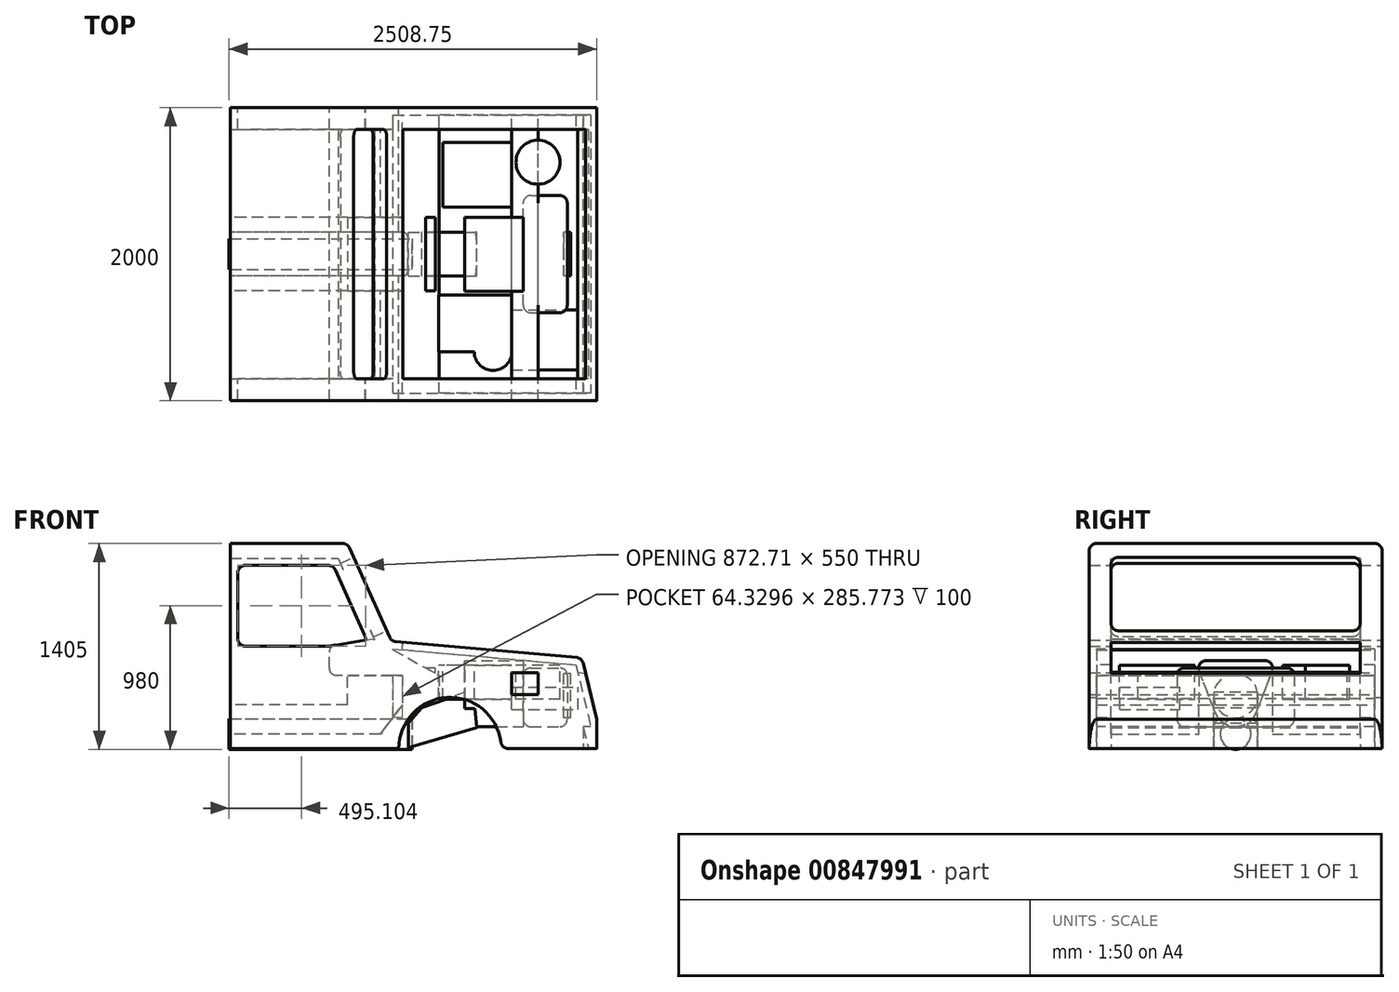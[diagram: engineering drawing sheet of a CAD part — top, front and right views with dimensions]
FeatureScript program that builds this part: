
annotation { "Feature Type Name" : "Feature", "Feature Type Description" : "" }
export const myFeature = defineFeature(function(context is Context, id is Id, definition is map)
    precondition{}
    {
        {
            var Q0;
            Q0=qCreatedBy(makeId("Front.planeOp"),FACE);
            var sketch = newSketch(context, id + "F0", { "sketchPlane" : qUnion([Q0])});
            skLineSegment(sketch, "E0", {"start": v(0, 1700) * mm, "end": v(767.65, 1700) * mm});
            skLineSegment(sketch, "E1", {"start": v(813.26, 1670.49) * mm, "end": v(1087.98, 1058.9) * mm});
            skLineSegment(sketch, "E2", {"start": v(1129.23, 1029.59) * mm, "end": v(2364.1, 921.55) * mm});
            skLineSegment(sketch, "E3", {"start": v(2408.38, 883.36) * mm, "end": v(2500, 500) * mm});
            skLineSegment(sketch, "E4", {"start": v(2500, 300) * mm, "end": v(1896.86, 300) * mm});
            skArc(sketch, "E5", {"start": v(1847.25, 343.75) * mm, "mid": v(1500, 650) * mm, "end": v(1152.75, 343.75) * mm});
            skLineSegment(sketch, "E6", {"start": v(1103.14, 300) * mm, "end": v(0, 300) * mm});
            skLineSegment(sketch, "E7", {"start": v(0, 1700) * mm, "end": v(0, 300) * mm});
            skLineSegment(sketch, "E8", {"start": v(100, 1550) * mm, "end": v(670.59, 1550) * mm});
            skLineSegment(sketch, "E9", {"start": v(716.2, 1520.49) * mm, "end": v(918.34, 1070.49) * mm});
            skLineSegment(sketch, "E10", {"start": v(872.73, 1000) * mm, "end": v(100, 1000) * mm});
            skLineSegment(sketch, "E11", {"start": v(50, 1500) * mm, "end": v(50, 1050) * mm});
            skPoint(sketch, "E12.orphan", {"position": v(0, 1000) * mm});
            skLineSegment(sketch, "E13", {"start": v(2500, 500) * mm, "end": v(2500, 300) * mm});
            skLineSegment(sketch, "E14", {"start": v(1100, 1032.14) * mm, "end": v(2504.74, 1032.14) * mm, "construction": true});
            skPoint(sketch, "E15.visualSharp", {"position": v(2400, 918.4) * mm});
            skArc(sketch, "E15.filletArc", {"start": v(2408.38, 883.36) * mm, "mid": v(2392.4, 909.6) * mm, "end": v(2364.1, 921.55) * mm});
            skPoint(sketch, "E16.visualSharp", {"position": v(1100, 1032.14) * mm});
            skArc(sketch, "E16.filletArc", {"start": v(1087.98, 1058.9) * mm, "mid": v(1104.62, 1038.64) * mm, "end": v(1129.23, 1029.59) * mm});
            skPoint(sketch, "E17.visualSharp", {"position": v(800, 1700) * mm});
            skArc(sketch, "E17.filletArc", {"start": v(813.26, 1670.49) * mm, "mid": v(794.8, 1691.98) * mm, "end": v(767.65, 1700) * mm});
            skPoint(sketch, "E18.visualSharp", {"position": v(702.94, 1550) * mm});
            skArc(sketch, "E18.filletArc", {"start": v(716.2, 1520.49) * mm, "mid": v(697.75, 1541.98) * mm, "end": v(670.59, 1550) * mm});
            skPoint(sketch, "E19.visualSharp", {"position": v(950, 1000) * mm});
            skArc(sketch, "E19.filletArc", {"start": v(872.73, 1000) * mm, "mid": v(914.7, 1022.84) * mm, "end": v(918.34, 1070.49) * mm});
            skPoint(sketch, "E20.visualSharp", {"position": v(50, 1000) * mm});
            skArc(sketch, "E20.filletArc", {"start": v(50, 1050) * mm, "mid": v(64.64, 1014.64) * mm, "end": v(100, 1000) * mm});
            skPoint(sketch, "E21.visualSharp", {"position": v(50, 1550) * mm});
            skArc(sketch, "E21.filletArc", {"start": v(100, 1550) * mm, "mid": v(64.64, 1535.36) * mm, "end": v(50, 1500) * mm});
            skPoint(sketch, "E22.visualSharp", {"position": v(1850, 300) * mm});
            skArc(sketch, "E22.filletArc", {"start": v(1847.25, 343.75) * mm, "mid": v(1863.8, 312.5) * mm, "end": v(1896.86, 300) * mm});
            skPoint(sketch, "E23.visualSharp", {"position": v(1150, 300) * mm});
            skArc(sketch, "E23.filletArc", {"start": v(1103.14, 300) * mm, "mid": v(1136.2, 312.5) * mm, "end": v(1152.75, 343.75) * mm});
            skSolve(sketch);
        }
        {
            var Q0;
            Q0=makeQuery(id+"F0.imprint","IMPRINT",FACE,{"disambiguationData":[TD([[makeQuery(id+"F0.imprint","IMPRINT",EDGE,{"derivedFrom":sQuery(id+"F0.wireOp",EDGE,"E0")}),-1.0]])]});
            extrude(context, id + "F1", {"entities" : qUnion([Q0]), "endBound" : BoundingType.SYMMETRIC, "depth" : 2000 * mm, "offsetDistance" : 25 * mm});
        }
        {
            var Q0;
            Q0=qCreatedBy(makeId("Front.planeOp"),FACE);
            var sketch = newSketch(context, id + "F2", { "sketchPlane" : qUnion([Q0])});
            skLineSegment(sketch, "E24", {"start": v(0, 1600) * mm, "end": v(735.3, 1600) * mm});
            skLineSegment(sketch, "E25", {"start": v(735.3, 1600) * mm, "end": v(1032.83, 937.64) * mm});
            skLineSegment(sketch, "E26", {"start": v(1032.83, 937.64) * mm, "end": v(2319.5, 825.07) * mm});
            skLineSegment(sketch, "E27", {"start": v(2319.5, 825.07) * mm, "end": v(2444.98, 300) * mm});
            skLineSegment(sketch, "E28", {"start": v(2444.98, 300) * mm, "end": v(0, 300) * mm});
            skLineSegment(sketch, "E29", {"start": v(0, 300) * mm, "end": v(0, 1600) * mm});
            skSolve(sketch);
        }
        {
            var Q0;
            Q0 = qSketchRegion(id + "F2", true);
            extrude(context, id + "F3", {"entities" : qUnion([Q0]), "operationType" : NewBodyOperationType.REMOVE, "endBound" : BoundingType.SYMMETRIC, "oppositeDirection" : true, "depth" : 1700 * mm, "offsetDistance" : 25 * mm});
        }
        {
            var Q0;
            Q0=makeQuery(id+"F1.opExtrude","SWEPT_FACE",FACE,{"disambiguationData":[OSD([sQuery(id+"F0.wireOp",EDGE,"E2")])]});
            var sketch = newSketch(context, id + "F4", { "sketchPlane" : qUnion([Q0])});
            skLineSegment(sketch, "E30.bottom", {"start": v(1085.2, 850) * mm, "end": v(2585.2, 850) * mm});
            skLineSegment(sketch, "E30.top", {"start": v(1085.2, -850) * mm, "end": v(2585.2, -850) * mm});
            skLineSegment(sketch, "E30.left", {"start": v(1085.2, 850) * mm, "end": v(1085.2, -850) * mm});
            skLineSegment(sketch, "E30.right", {"start": v(2585.2, 850) * mm, "end": v(2585.2, -850) * mm});
            skSolve(sketch);
        }
        {
            var Q0;
            Q0 = qSketchRegion(id + "F4", true);
            extrude(context, id + "F5", {"entities" : qUnion([Q0]), "operationType" : NewBodyOperationType.REMOVE, "oppositeDirection" : true, "depth" : 100 * mm, "offsetDistance" : 25 * mm});
        }
        {
            var Q0;
            Q0=qCreatedBy(makeId("Front.planeOp"),FACE);
            var sketch = newSketch(context, id + "F6", { "sketchPlane" : qUnion([Q0])});
            skLineSegment(sketch, "E31", {"start": v(1110.54, 981.03) * mm, "end": v(2359.75, 871.74) * mm});
            skLineSegment(sketch, "E32", {"start": v(2359.75, 871.74) * mm, "end": v(2460.54, 450) * mm});
            skLineSegment(sketch, "E33", {"start": v(2460.54, 450) * mm, "end": v(2410.54, 450) * mm});
            skLineSegment(sketch, "E34", {"start": v(2410.54, 450) * mm, "end": v(2410.54, 281.03) * mm});
            skLineSegment(sketch, "E35", {"start": v(2410.54, 281.03) * mm, "end": v(1110.54, 281.03) * mm});
            skLineSegment(sketch, "E36", {"start": v(1110.54, 281.03) * mm, "end": v(1110.54, 981.03) * mm});
            skSolve(sketch);
        }
        {
            var Q0;
            Q0 = qSketchRegion(id + "F6", true);
            extrude(context, id + "F7", {"entities" : qUnion([Q0]), "operationType" : NewBodyOperationType.REMOVE, "endBound" : BoundingType.SYMMETRIC, "oppositeDirection" : true, "depth" : 1900 * mm, "offsetDistance" : 25 * mm});
        }
        {
            var Q0;
            Q0=qCreatedBy(makeId("Front.planeOp"),FACE);
            var sketch = newSketch(context, id + "F8", { "sketchPlane" : qUnion([Q0])});
            skLineSegment(sketch, "E37.bottom", {"start": v(2050, 850) * mm, "end": v(2250, 850) * mm});
            skLineSegment(sketch, "E37.top", {"start": v(2050, 450) * mm, "end": v(2250, 450) * mm});
            skLineSegment(sketch, "E37.left", {"start": v(2000, 800) * mm, "end": v(2000, 500) * mm});
            skLineSegment(sketch, "E37.right", {"start": v(2300, 800) * mm, "end": v(2300, 500) * mm});
            skPoint(sketch, "E38.visualSharp", {"position": v(2300, 850) * mm});
            skArc(sketch, "E38.filletArc", {"start": v(2300, 800) * mm, "mid": v(2285.36, 835.36) * mm, "end": v(2250, 850) * mm});
            skPoint(sketch, "E39.visualSharp", {"position": v(2000, 850) * mm});
            skArc(sketch, "E39.filletArc", {"start": v(2050, 850) * mm, "mid": v(2014.64, 835.36) * mm, "end": v(2000, 800) * mm});
            skPoint(sketch, "E40.visualSharp", {"position": v(2000, 450) * mm});
            skArc(sketch, "E40.filletArc", {"start": v(2000, 500) * mm, "mid": v(2014.64, 464.64) * mm, "end": v(2050, 450) * mm});
            skPoint(sketch, "E41.visualSharp", {"position": v(2300, 450) * mm});
            skArc(sketch, "E41.filletArc", {"start": v(2250, 450) * mm, "mid": v(2285.36, 464.64) * mm, "end": v(2300, 500) * mm});
            skSolve(sketch);
        }
        {
            var Q0;
            Q0 = qSketchRegion(id + "F8", true);
            extrude(context, id + "F9", {"entities" : qUnion([Q0]), "endBound" : BoundingType.SYMMETRIC, "depth" : 800 * mm, "offsetDistance" : 25 * mm});
        }
        {
            var Q0;
            Q0=makeQuery(id+"F9.opExtrude","CAP_EDGE",EDGE,{"disambiguationData":[OSD([sQuery(id+"F8.wireOp",EDGE,"E37.bottom")])],"isStart":false});
            var Q1;
            Q1=makeQuery(id+"F9.opExtrude","CAP_EDGE",EDGE,{"disambiguationData":[OSD([sQuery(id+"F8.wireOp",EDGE,"E37.bottom")])],"isStart":true});
            fillet(context, id + "F10", {"entities" : qUnion([Q0, Q1]), "radius" : 50 * mm, "tangentPropagation" : true, "allowEdgeOverflow" : false});
        }
        {
            var Q0;
            Q0=makeQuery(id+"F9.opExtrude","SWEPT_FACE",FACE,{"disambiguationData":[OSD([sQuery(id+"F8.wireOp",EDGE,"E37.right")])]});
            var sketch = newSketch(context, id + "F11", { "sketchPlane" : qUnion([Q0])});
            skCircle(sketch, "E42", {"center": v(0, 660) * mm, "radius": 150 * mm});
            skPoint(sketch, "E42.centerSnap0", {"position": v(0, 800) * mm});
            skSolve(sketch);
        }
        {
            var Q0;
            Q0 = qSketchRegion(id + "F11", true);
            extrude(context, id + "F12", {"entities" : qUnion([Q0]), "endBound" : BoundingType.SYMMETRIC, "depth" : 50 * mm, "offsetDistance" : 25 * mm});
        }
        {
            var Q0;
            Q0=makeQuery(id+"F1.opExtrude","CAP_EDGE",EDGE,{"disambiguationData":[OSD([sQuery(id+"F0.wireOp",EDGE,"E1")])],"isStart":false});
            var Q1;
            Q1=makeQuery(id+"F1.opExtrude","CAP_EDGE",EDGE,{"disambiguationData":[OSD([sQuery(id+"F0.wireOp",EDGE,"E2")])],"isStart":true});
            fillet(context, id + "F13", {"entities" : qUnion([Q0, Q1]), "radius" : 50 * mm, "tangentPropagation" : true, "allowEdgeOverflow" : false});
        }
        {
            var Q0;
            Q0=makeQuery(id+"F1.opExtrude","SWEPT_FACE",FACE,{"disambiguationData":[OSD([sQuery(id+"F0.wireOp",EDGE,"E1")])]});
            var sketch = newSketch(context, id + "F14", { "sketchPlane" : qUnion([Q0])});
            skLineSegment(sketch, "E43.bottom", {"start": v(-800, 570.12) * mm, "end": v(800, 570.12) * mm});
            skLineSegment(sketch, "E43.top", {"start": v(-800, 1120.12) * mm, "end": v(800, 1120.12) * mm});
            skLineSegment(sketch, "E43.left", {"start": v(-850, 620.12) * mm, "end": v(-850, 1070.12) * mm});
            skLineSegment(sketch, "E43.right", {"start": v(850, 620.12) * mm, "end": v(850, 1070.12) * mm});
            skPoint(sketch, "E44.visualSharp", {"position": v(-850, 1120.12) * mm});
            skArc(sketch, "E44.filletArc", {"start": v(-800, 1120.12) * mm, "mid": v(-835.36, 1105.48) * mm, "end": v(-850, 1070.12) * mm});
            skPoint(sketch, "E45.visualSharp", {"position": v(-850, 570.12) * mm});
            skArc(sketch, "E45.filletArc", {"start": v(-850, 620.12) * mm, "mid": v(-835.36, 584.77) * mm, "end": v(-800, 570.12) * mm});
            skPoint(sketch, "E46.visualSharp", {"position": v(850, 1120.12) * mm});
            skArc(sketch, "E46.filletArc", {"start": v(850, 1070.12) * mm, "mid": v(835.36, 1105.48) * mm, "end": v(800, 1120.12) * mm});
            skPoint(sketch, "E47.visualSharp", {"position": v(850, 570.12) * mm});
            skArc(sketch, "E47.filletArc", {"start": v(800, 570.12) * mm, "mid": v(835.36, 584.77) * mm, "end": v(850, 620.12) * mm});
            skSolve(sketch);
        }
        {
            var Q0;
            Q0 = qSketchRegion(id + "F14", true);
            extrude(context, id + "F15", {"entities" : qUnion([Q0]), "operationType" : NewBodyOperationType.REMOVE, "oppositeDirection" : true, "depth" : 270 * mm, "offsetDistance" : 25 * mm});
        }
        {
            var Q0;
            Q0=qCreatedBy(makeId("Front.planeOp"),FACE);
            var sketch = newSketch(context, id + "F16", { "sketchPlane" : qUnion([Q0])});
            skLineSegment(sketch, "E48", {"start": v(974.87, 1050) * mm, "end": v(674.87, 1000) * mm});
            skLineSegment(sketch, "E49", {"start": v(674.87, 1000) * mm, "end": v(674.87, 800) * mm});
            skLineSegment(sketch, "E50", {"start": v(674.87, 800) * mm, "end": v(1174.87, 800) * mm});
            skLineSegment(sketch, "E51", {"start": v(1174.87, 800) * mm, "end": v(1174.87, 400) * mm});
            skLineSegment(sketch, "E52", {"start": v(1174.87, 400) * mm, "end": v(1424.87, 400) * mm});
            skLineSegment(sketch, "E53", {"start": v(1424.87, 400) * mm, "end": v(1424.87, 800) * mm});
            skLineSegment(sketch, "E54", {"start": v(1424.87, 800) * mm, "end": v(974.87, 1050) * mm});
            skLineSegment(sketch, "E55", {"start": v(1174.87, 400) * mm, "end": v(0, 400) * mm});
            skLineSegment(sketch, "E56", {"start": v(0, 400) * mm, "end": v(0, 300) * mm});
            skLineSegment(sketch, "E57", {"start": v(0, 300) * mm, "end": v(1424.87, 300) * mm});
            skLineSegment(sketch, "E58", {"start": v(1424.87, 300) * mm, "end": v(1424.87, 400) * mm});
            skLineSegment(sketch, "E59", {"start": v(1174.87, 600) * mm, "end": v(1024.87, 400) * mm});
            skSolve(sketch);
        }
        {
            var Q0;
            Q0 = qSketchRegion(id + "F16", true);
            extrude(context, id + "F17", {"entities" : qUnion([Q0]), "operationType" : NewBodyOperationType.ADD, "endBound" : BoundingType.SYMMETRIC, "depth" : 2000 * mm, "offsetDistance" : 25 * mm});
        }
        {
            var Q0;
            Q0=qCreatedBy(makeId("Front.planeOp"),FACE);
            var sketch = newSketch(context, id + "F18", { "sketchPlane" : qUnion([Q0])});
            skLineSegment(sketch, "E60.bottom", {"start": v(1400, 300) * mm, "end": v(0, 300) * mm});
            skLineSegment(sketch, "E60.top", {"start": v(1400, 600) * mm, "end": v(0, 600) * mm});
            skLineSegment(sketch, "E60.left", {"start": v(1400, 300) * mm, "end": v(1400, 600) * mm});
            skLineSegment(sketch, "E60.right", {"start": v(0, 300) * mm, "end": v(0, 600) * mm});
            skLineSegment(sketch, "E61.bottom", {"start": v(1400, 600) * mm, "end": v(800, 600) * mm});
            skLineSegment(sketch, "E61.top", {"start": v(1400, 850) * mm, "end": v(800, 850) * mm});
            skLineSegment(sketch, "E61.left", {"start": v(1400, 600) * mm, "end": v(1400, 850) * mm});
            skLineSegment(sketch, "E61.right", {"start": v(800, 600) * mm, "end": v(800, 850) * mm});
            skSolve(sketch);
        }
        {
            var Q0;
            Q0 = qSketchRegion(id + "F18", true);
            extrude(context, id + "F19", {"entities" : qUnion([Q0]), "operationType" : NewBodyOperationType.ADD, "endBound" : BoundingType.SYMMETRIC, "depth" : 500 * mm, "offsetDistance" : 25 * mm});
        }
        {
            var Q0;
            Q0=qCreatedBy(makeId("Front.planeOp"),FACE);
            var sketch = newSketch(context, id + "F20", { "sketchPlane" : qUnion([Q0])});
            skCircle(sketch, "E62", {"center": v(1500, 300) * mm, "radius": 350 * mm});
            skPoint(sketch, "E62.first.point", {"position": v(1617.77, 629.59) * mm});
            skPoint(sketch, "E62.second.point", {"position": v(1783.04, 505.89) * mm});
            skPoint(sketch, "E62.third.point", {"position": v(1714.36, 576.68) * mm});
            skSolve(sketch);
        }
        {
            var Q0;
            Q0 = qSketchRegion(id + "F20", true);
            extrude(context, id + "F21", {"entities" : qUnion([Q0]), "operationType" : NewBodyOperationType.REMOVE, "endBound" : BoundingType.SYMMETRIC, "depth" : 2620 * mm, "offsetDistance" : 25 * mm});
        }
        {
            var Q0;
            Q0=makeQuery(id+"F17.opExtrude","SWEPT_EDGE",EDGE,{"disambiguationData":[OSD([sQuery(id+"F16.wireOp",EDGE,"E49"),sQuery(id+"F16.wireOp",EDGE,"E50")])]});
            var Q1;
            {var subQ0=sQuery(id+"F16.wireOp",EDGE,"E48");var subQ1=sQuery(id+"F16.wireOp",EDGE,"E49");Q1=makeQuery(id+"F17.boolean.opBoolean","SPLIT",EDGE,{"disambiguationData":[topologyDisambiguationEdgeConnected([makeQuery(id+"F17.opExtrude","SWEPT_FACE",FACE,{"disambiguationData":[OSD([subQ0])]}),makeQuery(id+"F17.opExtrude","SWEPT_FACE",FACE,{"disambiguationData":[OSD([subQ1])]})])],"derivedFrom":makeQuery(id+"F17.opExtrude","SWEPT_EDGE",EDGE,{"disambiguationData":[OSD([subQ0,subQ1])]})});}
            fillet(context, id + "F22", {"entities" : qUnion([Q0, Q1]), "radius" : 50 * mm, "tangentPropagation" : true, "allowEdgeOverflow" : false});
        }
        {
            var Q0;
            Q0=makeQuery(id+"F19.boolean.opBoolean","MERGE",FACE,{"derivedFrom":[makeQuery(id+"F17.boolean.opBoolean","MERGE",FACE,{"derivedFrom":[makeQuery(id+"F1.opExtrude","SWEPT_FACE",FACE,{"disambiguationData":[OSD([sQuery(id+"F0.wireOp",EDGE,"E7")])]}),makeQuery(id+"F17.opExtrude","SWEPT_FACE",FACE,{"disambiguationData":[OSD([sQuery(id+"F16.wireOp",EDGE,"E56")])]})]}),makeQuery(id+"F19.opExtrude","SWEPT_FACE",FACE,{"disambiguationData":[OSD([sQuery(id+"F18.wireOp",EDGE,"E60.right")])]})]});
            var sketch = newSketch(context, id + "F23", { "sketchPlane" : qUnion([Q0])});
            skLineSegment(sketch, "E63.bottom", {"start": v(-150, 300) * mm, "end": v(150, 300) * mm});
            skLineSegment(sketch, "E63.top", {"start": v(-100, 500) * mm, "end": v(100, 500) * mm});
            skLineSegment(sketch, "E63.left", {"start": v(-150, 300) * mm, "end": v(-150, 450) * mm});
            skLineSegment(sketch, "E63.right", {"start": v(150, 300) * mm, "end": v(150, 450) * mm});
            skPoint(sketch, "E64.visualSharp", {"position": v(-150, 500) * mm});
            skArc(sketch, "E64.filletArc", {"start": v(-100, 500) * mm, "mid": v(-135.36, 485.36) * mm, "end": v(-150, 450) * mm});
            skPoint(sketch, "E65.visualSharp", {"position": v(150, 500) * mm});
            skArc(sketch, "E65.filletArc", {"start": v(150, 450) * mm, "mid": v(135.36, 485.36) * mm, "end": v(100, 500) * mm});
            skSolve(sketch);
        }
        {
            var Q0;
            Q0 = qSketchRegion(id + "F23", true);
            extrude(context, id + "F24", {"entities" : qUnion([Q0]), "operationType" : NewBodyOperationType.REMOVE, "oppositeDirection" : true, "depth" : 1380 * mm, "offsetDistance" : 25 * mm});
        }
        {
            var Q0;
            Q0=makeQuery(id+"F9.opExtrude","SWEPT_FACE",FACE,{"disambiguationData":[OSD([sQuery(id+"F8.wireOp",EDGE,"E37.left")])]});
            var sketch = newSketch(context, id + "F25", { "sketchPlane" : qUnion([Q0])});
            skLineSegment(sketch, "E66.bottom", {"start": v(-150, 900) * mm, "end": v(150, 900) * mm});
            skLineSegment(sketch, "E66.top", {"start": v(-150, 600) * mm, "end": v(0, 600) * mm});
            skLineSegment(sketch, "E66.left", {"start": v(-150, 900) * mm, "end": v(-150, 600) * mm});
            skLineSegment(sketch, "E66.right", {"start": v(150, 900) * mm, "end": v(150, 600) * mm});
            skArc(sketch, "E67", {"start": v(-150, 600) * mm, "mid": v(0, 450) * mm, "end": v(150, 600) * mm});
            skLineSegment(sketch, "E68", {"start": v(140.15, 546.53) * mm, "end": v(249.12, 832.18) * mm});
            skLineSegment(sketch, "E69", {"start": v(202.4, 900) * mm, "end": v(-202.4, 900) * mm});
            skLineSegment(sketch, "E70", {"start": v(-249.12, 832.18) * mm, "end": v(-140.15, 546.53) * mm});
            skPoint(sketch, "E71.visualSharp", {"position": v(-275, 900) * mm});
            skArc(sketch, "E71.filletArc", {"start": v(-202.4, 900) * mm, "mid": v(-243.59, 878.36) * mm, "end": v(-249.12, 832.18) * mm});
            skPoint(sketch, "E72.visualSharp", {"position": v(275, 900) * mm});
            skArc(sketch, "E72.filletArc", {"start": v(249.12, 832.18) * mm, "mid": v(243.59, 878.36) * mm, "end": v(202.4, 900) * mm});
            skSolve(sketch);
        }
        {
            var Q0;
            Q0 = qSketchRegion(id + "F25", true);
            extrude(context, id + "F26", {"entities" : qUnion([Q0]), "operationType" : NewBodyOperationType.ADD, "depth" : 400 * mm, "offsetDistance" : 25 * mm});
        }
        {
            var Q0;
            Q0=qCreatedBy(makeId("Front.planeOp"),FACE);
            var sketch = newSketch(context, id + "F27", { "sketchPlane" : qUnion([Q0])});
            skLineSegment(sketch, "E73", {"start": v(1660.21, 704.38) * mm, "end": v(1308.02, 580.71) * mm});
            skLineSegment(sketch, "E74", {"start": v(1216.25, 473.76) * mm, "end": v(1216.25, 307.42) * mm});
            skLineSegment(sketch, "E75", {"start": v(1681.49, 443.71) * mm, "end": v(1660.21, 704.38) * mm});
            skPoint(sketch, "E76.visualSharp", {"position": v(1216.25, 548.49) * mm});
            skPoint(sketch, "E77.visualSharp", {"position": v(1216.25, 307.42) * mm});
            skLineSegment(sketch, "E78", {"start": v(1216.25, 307.42) * mm, "end": v(1681.49, 443.71) * mm});
            skLineSegment(sketch, "E79", {"start": v(1216.25, 473.76) * mm, "end": v(1308.02, 580.71) * mm});
            skSolve(sketch);
        }
        {
            var Q0;
            Q0 = qSketchRegion(id + "F27", true);
            extrude(context, id + "F28", {"entities" : qUnion([Q0]), "operationType" : NewBodyOperationType.ADD, "endBound" : BoundingType.SYMMETRIC, "depth" : 300 * mm, "offsetDistance" : 25 * mm});
        }
        {
            var Q0;
            Q0=makeQuery(id+"F28.opExtrude","SWEPT_FACE",FACE,{"disambiguationData":[OSD([sQuery(id+"F27.wireOp",EDGE,"E74")])]});
            var sketch = newSketch(context, id + "F29", { "sketchPlane" : qUnion([Q0])});
            skCircle(sketch, "E80", {"center": v(0, 400) * mm, "radius": 105 * mm});
            skSolve(sketch);
        }
        {
            var Q0;
            Q0 = qSketchRegion(id + "F29", true);
            extrude(context, id + "F30", {"entities" : qUnion([Q0]), "depth" : 1225 * mm, "offsetDistance" : 25 * mm, "hasSecondDirection" : true, "secondDirectionOppositeDirection" : true, "secondDirectionDepth" : 25 * mm});
        }
        {
            var Q0;
            {var subQ0=sQuery(id+"F6.wireOp",EDGE,"E31");var subQ1=sQuery(id+"F6.wireOp",EDGE,"E32");var subQ2=sQuery(id+"F6.wireOp",EDGE,"E33");var subQ3=sQuery(id+"F6.wireOp",EDGE,"E34");var subQ4=sQuery(id+"F6.wireOp",EDGE,"E36");Q0=makeQuery(id+"F17.boolean.opBoolean","SPLIT",FACE,{"disambiguationData":[TD([makeQuery(id+"F1.opExtrude","SWEPT_FACE",FACE,{"disambiguationData":[OSD([sQuery(id+"F0.wireOp",EDGE,"E4")])]})])],"derivedFrom":makeQuery(id+"F7.boolean.opBoolean","COPY",FACE,{"derivedFrom":makeQuery(id+"F7.opExtrude","CAP_FACE",FACE,{"disambiguationData":[OSD([subQ0,subQ1,subQ2,subQ3,sQuery(id+"F6.wireOp",EDGE,"E35"),subQ4])],"isStart":false})})});}
            var sketch = newSketch(context, id + "F31", { "sketchPlane" : qUnion([Q0])});
            skLineSegment(sketch, "E81.bottom", {"start": v(1920, 818.18) * mm, "end": v(2100, 818.18) * mm});
            skLineSegment(sketch, "E81.top", {"start": v(1920, 668.18) * mm, "end": v(2100, 668.18) * mm});
            skLineSegment(sketch, "E81.left", {"start": v(1920, 818.18) * mm, "end": v(1920, 668.18) * mm});
            skLineSegment(sketch, "E81.right", {"start": v(2100, 818.18) * mm, "end": v(2100, 668.18) * mm});
            skSolve(sketch);
        }
        {
            var Q0;
            Q0 = qSketchRegion(id + "F31", true);
            extrude(context, id + "F32", {"entities" : qUnion([Q0]), "depth" : 1950 * mm, "offsetDistance" : 25 * mm});
        }
        {
            var Q0;
            Q0=makeQuery(id+"F32.opExtrude","SWEPT_FACE",FACE,{"disambiguationData":[OSD([sQuery(id+"F31.wireOp",EDGE,"E81.bottom")])]});
            var sketch = newSketch(context, id + "F33", { "sketchPlane" : qUnion([Q0])});
            skCircle(sketch, "E82", {"center": v(2100, 627.4) * mm, "radius": 150 * mm});
            skLineSegment(sketch, "E83.bottom", {"start": v(1922.12, 320.16) * mm, "end": v(1451.25, 320.16) * mm});
            skLineSegment(sketch, "E83.top", {"start": v(1922.12, 761.9) * mm, "end": v(1451.25, 761.9) * mm});
            skLineSegment(sketch, "E83.left", {"start": v(1922.12, 320.16) * mm, "end": v(1922.12, 761.9) * mm});
            skLineSegment(sketch, "E83.right", {"start": v(1451.25, 320.16) * mm, "end": v(1451.25, 761.9) * mm});
            skArc(sketch, "E84", {"start": v(1665.04, -665.22) * mm, "mid": v(1793.58, -793.76) * mm, "end": v(1922.12, -665.22) * mm});
            skLineSegment(sketch, "E85.top", {"start": v(1922.12, -277.87) * mm, "end": v(1422.21, -277.87) * mm});
            skLineSegment(sketch, "E85.left", {"start": v(1922.12, -665.22) * mm, "end": v(1922.12, -277.87) * mm});
            skLineSegment(sketch, "E85.right", {"start": v(1422.21, -665.22) * mm, "end": v(1422.21, -277.87) * mm});
            skLineSegment(sketch, "E86.trimOffspring", {"start": v(1665.04, -665.22) * mm, "end": v(1422.21, -665.22) * mm});
            skSolve(sketch);
        }
        {
            var Q0;
            Q0 = qSketchRegion(id + "F33", true);
            extrude(context, id + "F34", {"entities" : qUnion([Q0]), "oppositeDirection" : true, "depth" : 180 * mm, "offsetDistance" : 25 * mm, "hasSecondDirection" : true, "secondDirectionOppositeDirection" : false, "secondDirectionDepth" : 50 * mm});
        }
        {
            var Q0;
            Q0=makeQuery(id+"F32.opExtrude","SWEPT_FACE",FACE,{"disambiguationData":[OSD([sQuery(id+"F31.wireOp",EDGE,"E81.top")])]});
            var sketch = newSketch(context, id + "F35", { "sketchPlane" : qUnion([Q0])});
            skLineSegment(sketch, "E87.bottom", {"start": v(1920, 791.23) * mm, "end": v(2375.68, 791.23) * mm});
            skLineSegment(sketch, "E87.top", {"start": v(1920, 381.3) * mm, "end": v(2375.68, 381.3) * mm});
            skLineSegment(sketch, "E87.left", {"start": v(1920, 791.23) * mm, "end": v(1920, 381.3) * mm});
            skLineSegment(sketch, "E87.right", {"start": v(2375.68, 791.23) * mm, "end": v(2375.68, 381.3) * mm});
            skSolve(sketch);
        }
        {
            var Q0;
            Q0 = qSketchRegion(id + "F35", true);
            extrude(context, id + "F36", {"entities" : qUnion([Q0]), "depth" : 100 * mm, "offsetDistance" : 25 * mm, "hasSecondDirection" : true, "secondDirectionOppositeDirection" : true, "secondDirectionDepth" : 50 * mm});
        }
    });
